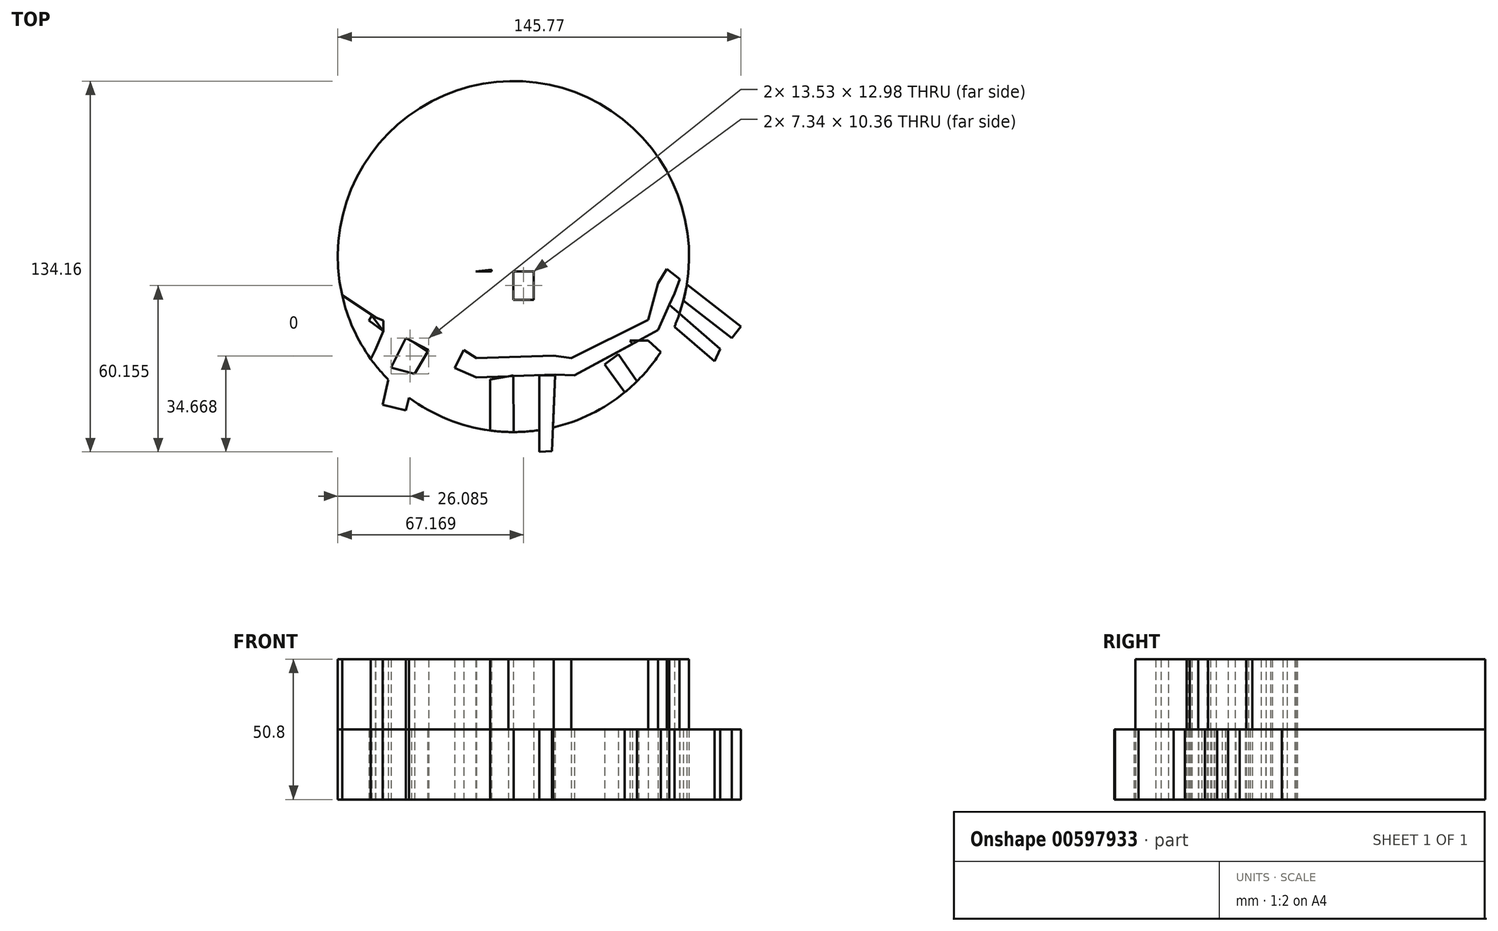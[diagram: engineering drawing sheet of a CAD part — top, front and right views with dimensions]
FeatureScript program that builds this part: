
annotation { "Feature Type Name" : "Feature", "Feature Type Description" : "" }
export const myFeature = defineFeature(function(context is Context, id is Id, definition is map)
    precondition{}
    {
        {
            var Q0;
            Q0=qCreatedBy(makeId("Top.planeOp"),FACE);
            var sketch = newSketch(context, id + "F0", { "sketchPlane" : qUnion([Q0])});
            skCircle(sketch, "E0", {"center": v(0, 0) * mm, "radius": 63.5 * mm});
            skLineSegment(sketch, "E1", {"start": v(-44.18, -40.15) * mm, "end": v(-47.34, -53.68) * mm});
            skLineSegment(sketch, "E2", {"start": v(-47.34, -53.68) * mm, "end": v(-38.86, -55.66) * mm});
            skLineSegment(sketch, "E3", {"start": v(-38.86, -55.66) * mm, "end": v(-35.77, -42.48) * mm});
            skLineSegment(sketch, "E4", {"start": v(-35.77, -42.48) * mm, "end": v(-44.18, -40.15) * mm});
            skLineSegment(sketch, "E5", {"start": v(-49.93, -33.82) * mm, "end": v(-57.7, -49.65) * mm});
            skLineSegment(sketch, "E6", {"start": v(-57.7, -49.36) * mm, "end": v(-64.61, -45.62) * mm});
            skLineSegment(sketch, "E7", {"start": v(-64.61, -44.75) * mm, "end": v(-52.52, -22.88) * mm});
            skLineSegment(sketch, "E8", {"start": v(-49.93, -33.82) * mm, "end": v(-47.06, -26.9) * mm});
            skLineSegment(sketch, "E9", {"start": v(-52.24, -23.17) * mm, "end": v(-47.06, -26.9) * mm});
            skLineSegment(sketch, "E10", {"start": v(-44.18, -40.15) * mm, "end": v(-38.86, -29.5) * mm});
            skLineSegment(sketch, "E11", {"start": v(-35.77, -42.48) * mm, "end": v(-30.65, -33.82) * mm});
            skLineSegment(sketch, "E12", {"start": v(-38.86, -29.5) * mm, "end": v(-30.65, -33.82) * mm});
            skLineSegment(sketch, "E13", {"start": v(-61.93, -14.03) * mm, "end": v(-21.44, -40.72) * mm});
            skLineSegment(sketch, "E14", {"start": v(-21.44, -40.72) * mm, "end": v(-17.99, -33.82) * mm});
            skLineSegment(sketch, "E15", {"start": v(-17.99, -33.82) * mm, "end": v(-62.85, -9.04) * mm});
            skLineSegment(sketch, "E16", {"start": v(-62.85, -9.04) * mm, "end": v(-64.83, -12.99) * mm});
            skLineSegment(sketch, "E17", {"start": v(-65.19, -12.8) * mm, "end": v(-61.93, -14.03) * mm});
            skLineSegment(sketch, "E18", {"start": v(-52.24, -23.17) * mm, "end": v(-51.28, -21.43) * mm});
            skPoint(sketch, "E18.endSnap0", {"position": v(-40.42, -21.43) * mm});
            skLineSegment(sketch, "E19", {"start": v(-51.28, -21.43) * mm, "end": v(-47.06, -26.9) * mm});
            skLineSegment(sketch, "E20", {"start": v(-47.06, -26.9) * mm, "end": v(-47.06, -23.17) * mm});
            skLineSegment(sketch, "E21", {"start": v(-47.06, -23.17) * mm, "end": v(-51.28, -21.43) * mm});
            skLineSegment(sketch, "E22", {"start": v(-8.5, -44.47) * mm, "end": v(-8.5, -70.66) * mm});
            skLineSegment(sketch, "E23", {"start": v(-8.2, -70.66) * mm, "end": v(0, -70.37) * mm});
            skLineSegment(sketch, "E24", {"start": v(0.14, -70.08) * mm, "end": v(0, -43.03) * mm});
            skLineSegment(sketch, "E25", {"start": v(0, -43.03) * mm, "end": v(-8.5, -44.47) * mm});
            skLineSegment(sketch, "E26", {"start": v(9.35, -43.03) * mm, "end": v(9.35, -70.66) * mm});
            skLineSegment(sketch, "E27", {"start": v(9.35, -70.66) * mm, "end": v(13.96, -70.37) * mm});
            skLineSegment(sketch, "E28", {"start": v(9.35, -43.03) * mm, "end": v(15.1, -43.03) * mm});
            skLineSegment(sketch, "E29", {"start": v(15.1, -42.74) * mm, "end": v(13.96, -70.37) * mm});
            skLineSegment(sketch, "E30", {"start": v(15.1, -42.74) * mm, "end": v(-13.38, -43.75) * mm});
            skPoint(sketch, "E30.endSnap0", {"position": v(-4.25, -43.75) * mm});
            skLineSegment(sketch, "E31", {"start": v(-13.38, -44.75) * mm, "end": v(-13.38, -36.7) * mm});
            skLineSegment(sketch, "E32", {"start": v(-13.38, -36.7) * mm, "end": v(14.53, -35.83) * mm});
            skLineSegment(sketch, "E33", {"start": v(14.53, -35.83) * mm, "end": v(15.1, -42.74) * mm});
            skLineSegment(sketch, "E34", {"start": v(-17.99, -33.82) * mm, "end": v(-13.38, -36.7) * mm});
            skLineSegment(sketch, "E35", {"start": v(-21.44, -40.15) * mm, "end": v(-13.38, -43.75) * mm});
            skLineSegment(sketch, "E36", {"start": v(15.1, -42.74) * mm, "end": v(22.02, -43.03) * mm});
            skLineSegment(sketch, "E37", {"start": v(22.02, -43.03) * mm, "end": v(20.94, -36.7) * mm});
            skLineSegment(sketch, "E38", {"start": v(20.94, -36.7) * mm, "end": v(14.53, -35.83) * mm});
            skLineSegment(sketch, "E39", {"start": v(32.95, -39) * mm, "end": v(47.92, -59.72) * mm});
            skLineSegment(sketch, "E40", {"start": v(47.92, -59.72) * mm, "end": v(52.34, -56.52) * mm});
            skLineSegment(sketch, "E41", {"start": v(32.95, -39) * mm, "end": v(37.97, -35.38) * mm});
            skLineSegment(sketch, "E42", {"start": v(37.97, -35.38) * mm, "end": v(52.52, -56.55) * mm});
            skLineSegment(sketch, "E43", {"start": v(48.78, -30.36) * mm, "end": v(67.5, -47.92) * mm});
            skLineSegment(sketch, "E44", {"start": v(67.2, -47.92) * mm, "end": v(64.04, -51.37) * mm});
            skLineSegment(sketch, "E45", {"start": v(63.75, -51.37) * mm, "end": v(44.18, -33.24) * mm});
            skLineSegment(sketch, "E46", {"start": v(48.78, -30.36) * mm, "end": v(44.18, -33.24) * mm});
            skLineSegment(sketch, "E47", {"start": v(52.24, -26.62) * mm, "end": v(22.02, -43.03) * mm});
            skLineSegment(sketch, "E48", {"start": v(52.24, -26.62) * mm, "end": v(48.78, -22.88) * mm});
            skLineSegment(sketch, "E49", {"start": v(48.78, -22.88) * mm, "end": v(20.94, -36.7) * mm});
            skLineSegment(sketch, "E50", {"start": v(44.18, -33.24) * mm, "end": v(42.1, -30.36) * mm});
            skLineSegment(sketch, "E51", {"start": v(42.1, -30.36) * mm, "end": v(48.78, -30.36) * mm});
            skLineSegment(sketch, "E52", {"start": v(52.24, -26.62) * mm, "end": v(58.28, -13.38) * mm});
            skLineSegment(sketch, "E53", {"start": v(48.78, -22.88) * mm, "end": v(52.24, -9.64) * mm});
            skLineSegment(sketch, "E54", {"start": v(52.24, -9.64) * mm, "end": v(58.28, -13.38) * mm});
            skLineSegment(sketch, "E55", {"start": v(55.26, -22.88) * mm, "end": v(72.67, -37.85) * mm});
            skPoint(sketch, "E55.startSnap0", {"position": v(55.26, -20) * mm});
            skLineSegment(sketch, "E56", {"start": v(72.67, -37.85) * mm, "end": v(74.7, -33.4) * mm});
            skLineSegment(sketch, "E57", {"start": v(74.7, -33.4) * mm, "end": v(56.4, -17.5) * mm});
            skLineSegment(sketch, "E58", {"start": v(56.4, -17.5) * mm, "end": v(58.28, -13.38) * mm});
            skLineSegment(sketch, "E59", {"start": v(58.28, -13.38) * mm, "end": v(79, -29.5) * mm});
            skLineSegment(sketch, "E60", {"start": v(79, -29.5) * mm, "end": v(82.27, -25.3) * mm});
            skLineSegment(sketch, "E61", {"start": v(82.27, -25.3) * mm, "end": v(60.32, -8.22) * mm});
            skLineSegment(sketch, "E62", {"start": v(60.3, -7.91) * mm, "end": v(58.28, -13.38) * mm});
            skLineSegment(sketch, "E63", {"start": v(52.24, -9.64) * mm, "end": v(55.48, -4.4) * mm});
            skLineSegment(sketch, "E64", {"start": v(55.11, -4.17) * mm, "end": v(60.32, -8.22) * mm});
            skLineSegment(sketch, "E65", {"start": v(-13.67, -5.32) * mm, "end": v(-13.67, -14.53) * mm});
            skLineSegment(sketch, "E66", {"start": v(-13.38, -14.82) * mm, "end": v(-7.91, -14.82) * mm});
            skLineSegment(sketch, "E67", {"start": v(-7.91, -14.82) * mm, "end": v(-7.91, -4.75) * mm});
            skLineSegment(sketch, "E68", {"start": v(-7.91, -4.75) * mm, "end": v(-13.67, -5.32) * mm});
            skLineSegment(sketch, "E69", {"start": v(0, -5.32) * mm, "end": v(0, -15.69) * mm});
            skLineSegment(sketch, "E70", {"start": v(0, -15.69) * mm, "end": v(7.34, -15.69) * mm});
            skLineSegment(sketch, "E71", {"start": v(7.34, -15.69) * mm, "end": v(7.34, -5.32) * mm});
            skLineSegment(sketch, "E72", {"start": v(7.34, -5.32) * mm, "end": v(0, -5.32) * mm});
            skLineSegment(sketch, "E73", {"start": v(-17.99, -5.32) * mm, "end": v(13.96, -5.32) * mm});
            skPoint(sketch, "E73.endSnap0", {"position": v(3.67, -5.32) * mm});
            skLineSegment(sketch, "E74", {"start": v(13.96, -5.04) * mm, "end": v(13.38, 0) * mm});
            skLineSegment(sketch, "E75", {"start": v(13.67, 1) * mm, "end": v(-18.56, 1) * mm});
            skLineSegment(sketch, "E76", {"start": v(-18.56, 1) * mm, "end": v(-17.99, -5.32) * mm});
            skSolve(sketch);
        }
        {
            var Q0;
            {var subQ0=sQuery(id+"F0.wireOp",EDGE,"E8");Q0=makeQuery(id+"F0.imprint","IMPRINT",FACE,{"disambiguationData":[TD([[makeQuery(id+"F0.imprint","IMPRINT",EDGE,{"derivedFrom":subQ0}),1.0]])]});}
            var Q1;
            {var subQ0=sQuery(id+"F0.wireOp",EDGE,"E69");Q1=makeQuery(id+"F0.imprint","IMPRINT",FACE,{"disambiguationData":[TD([[makeQuery(id+"F0.imprint","IMPRINT",EDGE,{"derivedFrom":subQ0}),1.0]])]});}
            var Q2;
            {var subQ5=sQuery(id+"F0.wireOp",EDGE,"E4");Q2=makeQuery(id+"F0.imprint","IMPRINT",FACE,{"disambiguationData":[TD([[makeQuery(id+"F0.imprint","IMPRINT",EDGE,{"derivedFrom":subQ5}),-1.0]])]});}
            var Q3;
            {var subQ9=sQuery(id+"F0.wireOp",EDGE,"E32");Q3=makeQuery(id+"F0.imprint","IMPRINT",FACE,{"disambiguationData":[TD([[makeQuery(id+"F0.imprint","IMPRINT",EDGE,{"derivedFrom":subQ9}),-1.0]])]});}
            var Q4;
            {var subQ0=sQuery(id+"F0.wireOp",EDGE,"E34");Q4=makeQuery(id+"F0.imprint","IMPRINT",FACE,{"disambiguationData":[TD([[makeQuery(id+"F0.imprint","IMPRINT",EDGE,{"derivedFrom":subQ0}),-1.0]])]});}
            var Q5;
            {var subQ1=sQuery(id+"F0.wireOp",EDGE,"E22");var subQ6=sQuery(id+"F0.wireOp",EDGE,"E0");var subQ9=makeQuery(id+"F0.imprint","INTERSECT",VERTEX,{"derivedFrom":[subQ6,subQ1]});Q5=makeQuery(id+"F0.imprint","IMPRINT",FACE,{"disambiguationData":[TD([[makeQuery(id+"F0.imprint","IMPRINT",EDGE,{"disambiguationData":[TD([[subQ9,-1.0]])],"derivedFrom":subQ6}),1.0]])]});}
            var Q6;
            {var subQ0=sQuery(id+"F0.wireOp",EDGE,"E26");var subQ1=sQuery(id+"F0.wireOp",EDGE,"E0");var subQ2=makeQuery(id+"F0.imprint","INTERSECT",VERTEX,{"derivedFrom":[subQ1,subQ0]});Q6=makeQuery(id+"F0.imprint","IMPRINT",FACE,{"disambiguationData":[TD([[makeQuery(id+"F0.imprint","IMPRINT",EDGE,{"disambiguationData":[TD([[subQ2,-1.0]])],"derivedFrom":subQ1}),1.0]])]});}
            var Q7;
            {var subQ1=sQuery(id+"F0.wireOp",EDGE,"E37");Q7=makeQuery(id+"F0.imprint","IMPRINT",FACE,{"disambiguationData":[TD([[makeQuery(id+"F0.imprint","IMPRINT",EDGE,{"derivedFrom":subQ1}),-1.0]])]});}
            var Q8;
            Q8=makeQuery(id+"F0.imprint","IMPRINT",FACE,{"disambiguationData":[TD([[makeQuery(id+"F0.imprint","IMPRINT",EDGE,{"derivedFrom":sQuery(id+"F0.wireOp",EDGE,"E33")}),1.0]])]});
            var Q9;
            {var subQ5=sQuery(id+"F0.wireOp",EDGE,"E41");Q9=makeQuery(id+"F0.imprint","IMPRINT",FACE,{"disambiguationData":[TD([[makeQuery(id+"F0.imprint","IMPRINT",EDGE,{"derivedFrom":subQ5}),-1.0]])]});}
            var Q10;
            {var subQ5=sQuery(id+"F0.wireOp",EDGE,"E56");Q10=makeQuery(id+"F0.imprint","IMPRINT",FACE,{"disambiguationData":[TD([[makeQuery(id+"F0.imprint","IMPRINT",EDGE,{"derivedFrom":subQ5}),1.0]])]});}
            var Q11;
            {var subQ5=sQuery(id+"F0.wireOp",EDGE,"E60");Q11=makeQuery(id+"F0.imprint","IMPRINT",FACE,{"disambiguationData":[TD([[makeQuery(id+"F0.imprint","IMPRINT",EDGE,{"derivedFrom":subQ5}),1.0]])]});}
            var Q12;
            {var subQ0=sQuery(id+"F0.wireOp",EDGE,"E54");Q12=makeQuery(id+"F0.imprint","IMPRINT",FACE,{"disambiguationData":[TD([[makeQuery(id+"F0.imprint","IMPRINT",EDGE,{"derivedFrom":subQ0}),1.0]])]});}
            var Q13;
            Q13=makeQuery(id+"F0.imprint","IMPRINT",FACE,{"disambiguationData":[TD([[makeQuery(id+"F0.imprint","IMPRINT",EDGE,{"derivedFrom":sQuery(id+"F0.wireOp",EDGE,"E48")}),-1.0]])]});
            var Q14;
            {var subQ5=sQuery(id+"F0.wireOp",EDGE,"E27");Q14=makeQuery(id+"F0.imprint","IMPRINT",FACE,{"disambiguationData":[TD([[makeQuery(id+"F0.imprint","IMPRINT",EDGE,{"derivedFrom":subQ5}),1.0]])]});}
            extrude(context, id + "F1", {"entities" : qUnion([Q0, Q1, Q2, Q3, Q4, Q5, Q6, Q7, Q8, Q9, Q10, Q11, Q12, Q13, Q14]), "depth" : 25.4 * mm, "offsetDistance" : 25.4 * mm});
        }
        {
            var Q0;
            {var subQ10=sQuery(id+"F0.wireOp",EDGE,"E15");Q0=makeQuery(id+"F0.imprint","IMPRINT",FACE,{"disambiguationData":[TD([[makeQuery(id+"F0.imprint","IMPRINT",EDGE,{"derivedFrom":subQ10}),-1.0]])]});}
            var Q1;
            {var subQ0=sQuery(id+"F0.wireOp",EDGE,"E15");Q1=makeQuery(id+"F0.imprint","IMPRINT",FACE,{"disambiguationData":[TD([[makeQuery(id+"F0.imprint","IMPRINT",EDGE,{"derivedFrom":subQ0}),1.0]])]});}
            var Q2;
            {var subQ5=sQuery(id+"F0.wireOp",EDGE,"E2");Q2=makeQuery(id+"F0.imprint","IMPRINT",FACE,{"disambiguationData":[TD([[makeQuery(id+"F0.imprint","IMPRINT",EDGE,{"derivedFrom":subQ5}),1.0]])]});}
            var Q3;
            {var subQ5=sQuery(id+"F0.wireOp",EDGE,"E4");Q3=makeQuery(id+"F0.imprint","IMPRINT",FACE,{"disambiguationData":[TD([[makeQuery(id+"F0.imprint","IMPRINT",EDGE,{"derivedFrom":subQ5}),1.0]])]});}
            var Q4;
            {var subQ5=sQuery(id+"F0.wireOp",EDGE,"E46");Q4=makeQuery(id+"F0.imprint","IMPRINT",FACE,{"disambiguationData":[TD([[makeQuery(id+"F0.imprint","IMPRINT",EDGE,{"derivedFrom":subQ5}),1.0]])]});}
            var Q5;
            {var subQ0=sQuery(id+"F0.wireOp",EDGE,"E52");Q5=makeQuery(id+"F0.imprint","IMPRINT",FACE,{"disambiguationData":[TD([[makeQuery(id+"F0.imprint","IMPRINT",EDGE,{"derivedFrom":subQ0}),-1.0]])]});}
            var Q6;
            {var subQ3=sQuery(id+"F0.wireOp",EDGE,"E0");var subQ6=sQuery(id+"F0.wireOp",EDGE,"E59");var subQ9=makeQuery(id+"F0.imprint","INTERSECT",VERTEX,{"derivedFrom":[subQ3,subQ6]});Q6=makeQuery(id+"F0.imprint","IMPRINT",FACE,{"disambiguationData":[TD([[makeQuery(id+"F0.imprint","IMPRINT",EDGE,{"disambiguationData":[TD([[subQ9,-1.0]])],"derivedFrom":subQ3}),1.0]])]});}
            var Q7;
            {var subQ3=sQuery(id+"F0.wireOp",EDGE,"E0");var subQ6=sQuery(id+"F0.wireOp",EDGE,"E59");var subQ9=makeQuery(id+"F0.imprint","INTERSECT",VERTEX,{"derivedFrom":[subQ3,subQ6]});Q7=makeQuery(id+"F0.imprint","IMPRINT",FACE,{"disambiguationData":[TD([[makeQuery(id+"F0.imprint","IMPRINT",EDGE,{"disambiguationData":[TD([[subQ9,-1.0]])],"derivedFrom":subQ3}),1.0]])]});}
            var Q8;
            {var subQ5=sQuery(id+"F0.wireOp",EDGE,"E58");Q8=makeQuery(id+"F0.imprint","IMPRINT",FACE,{"disambiguationData":[TD([[makeQuery(id+"F0.imprint","IMPRINT",EDGE,{"derivedFrom":subQ5}),-1.0]])]});}
            var Q9;
            {var subQ0=sQuery(id+"F0.wireOp",EDGE,"E46");Q9=makeQuery(id+"F0.imprint","IMPRINT",FACE,{"disambiguationData":[TD([[makeQuery(id+"F0.imprint","IMPRINT",EDGE,{"derivedFrom":subQ0}),-1.0]])]});}
            var Q10;
            {var subQ0=sQuery(id+"F0.wireOp",EDGE,"E8");Q10=makeQuery(id+"F0.imprint","IMPRINT",FACE,{"disambiguationData":[TD([[makeQuery(id+"F0.imprint","IMPRINT",EDGE,{"derivedFrom":subQ0}),-1.0]])]});}
            var Q11;
            {var subQ7=sQuery(id+"F0.wireOp",EDGE,"E0");var subQ9=sQuery(id+"F0.wireOp",EDGE,"E22");var subQ10=makeQuery(id+"F0.imprint","INTERSECT",VERTEX,{"derivedFrom":[subQ7,subQ9]});Q11=makeQuery(id+"F0.imprint","IMPRINT",FACE,{"disambiguationData":[TD([[makeQuery(id+"F0.imprint","IMPRINT",EDGE,{"disambiguationData":[TD([[subQ10,1.0]])],"derivedFrom":subQ7}),1.0]])]});}
            var Q12;
            {var subQ5=sQuery(id+"F0.wireOp",EDGE,"E0");var subQ7=sQuery(id+"F0.wireOp",EDGE,"E24");var subQ8=makeQuery(id+"F0.imprint","INTERSECT",VERTEX,{"derivedFrom":[subQ5,subQ7]});Q12=makeQuery(id+"F0.imprint","IMPRINT",FACE,{"disambiguationData":[TD([[makeQuery(id+"F0.imprint","IMPRINT",EDGE,{"disambiguationData":[TD([[subQ8,-1.0]])],"derivedFrom":subQ5}),1.0]])]});}
            var Q13;
            {var subQ12=sQuery(id+"F0.wireOp",EDGE,"E36");Q13=makeQuery(id+"F0.imprint","IMPRINT",FACE,{"disambiguationData":[TD([[makeQuery(id+"F0.imprint","IMPRINT",EDGE,{"derivedFrom":subQ12}),-1.0]])]});}
            extrude(context, id + "F2", {"entities" : qUnion([Q0, Q1, Q2, Q3, Q4, Q5, Q6, Q7, Q8, Q9, Q10, Q11, Q12, Q13]), "depth" : 25.4 * mm, "offsetDistance" : 25.4 * mm});
        }
        {
            var Q0;
            Q0=makeQuery(id+"F0.imprint","IMPRINT",FACE,{"disambiguationData":[TD([[makeQuery(id+"F0.imprint","IMPRINT",EDGE,{"derivedFrom":sQuery(id+"F0.wireOp",EDGE,"E9")}),1.0]])]});
            var Q1;
            Q1=makeQuery(id+"F2.opExtrude","CAP_FACE",FACE,{"disambiguationData":[OSD([sQuery(id+"F0.wireOp",EDGE,"E0"),sQuery(id+"F0.wireOp",EDGE,"E1"),sQuery(id+"F0.wireOp",EDGE,"E2"),sQuery(id+"F0.wireOp",EDGE,"E3"),sQuery(id+"F0.wireOp",EDGE,"E4"),sQuery(id+"F0.wireOp",EDGE,"E5"),sQuery(id+"F0.wireOp",EDGE,"E8"),sQuery(id+"F0.wireOp",EDGE,"E10"),sQuery(id+"F0.wireOp",EDGE,"E11"),sQuery(id+"F0.wireOp",EDGE,"E12"),sQuery(id+"F0.wireOp",EDGE,"E13"),sQuery(id+"F0.wireOp",EDGE,"E14"),sQuery(id+"F0.wireOp",EDGE,"E20"),sQuery(id+"F0.wireOp",EDGE,"E21"),sQuery(id+"F0.wireOp",EDGE,"E22"),sQuery(id+"F0.wireOp",EDGE,"E24"),sQuery(id+"F0.wireOp",EDGE,"E25"),sQuery(id+"F0.wireOp",EDGE,"E26"),sQuery(id+"F0.wireOp",EDGE,"E28"),sQuery(id+"F0.wireOp",EDGE,"E29"),sQuery(id+"F0.wireOp",EDGE,"E30"),sQuery(id+"F0.wireOp",EDGE,"E32"),sQuery(id+"F0.wireOp",EDGE,"E34"),sQuery(id+"F0.wireOp",EDGE,"E35"),sQuery(id+"F0.wireOp",EDGE,"E36"),sQuery(id+"F0.wireOp",EDGE,"E38"),sQuery(id+"F0.wireOp",EDGE,"E39"),sQuery(id+"F0.wireOp",EDGE,"E41"),sQuery(id+"F0.wireOp",EDGE,"E42"),sQuery(id+"F0.wireOp",EDGE,"E47"),sQuery(id+"F0.wireOp",EDGE,"E49"),sQuery(id+"F0.wireOp",EDGE,"E52"),sQuery(id+"F0.wireOp",EDGE,"E53"),sQuery(id+"F0.wireOp",EDGE,"E58"),sQuery(id+"F0.wireOp",EDGE,"E62"),sQuery(id+"F0.wireOp",EDGE,"E63"),sQuery(id+"F0.wireOp",EDGE,"E64"),sQuery(id+"F0.wireOp",EDGE,"E67"),sQuery(id+"F0.wireOp",EDGE,"E68"),sQuery(id+"F0.wireOp",EDGE,"E69"),sQuery(id+"F0.wireOp",EDGE,"E70"),sQuery(id+"F0.wireOp",EDGE,"E71"),sQuery(id+"F0.wireOp",EDGE,"E73")])],"isStart":false});
            extrude(context, id + "F3", {"entities" : qUnion([Q0, Q1]), "depth" : 25.4 * mm, "offsetDistance" : 25.4 * mm});
        }
    });
